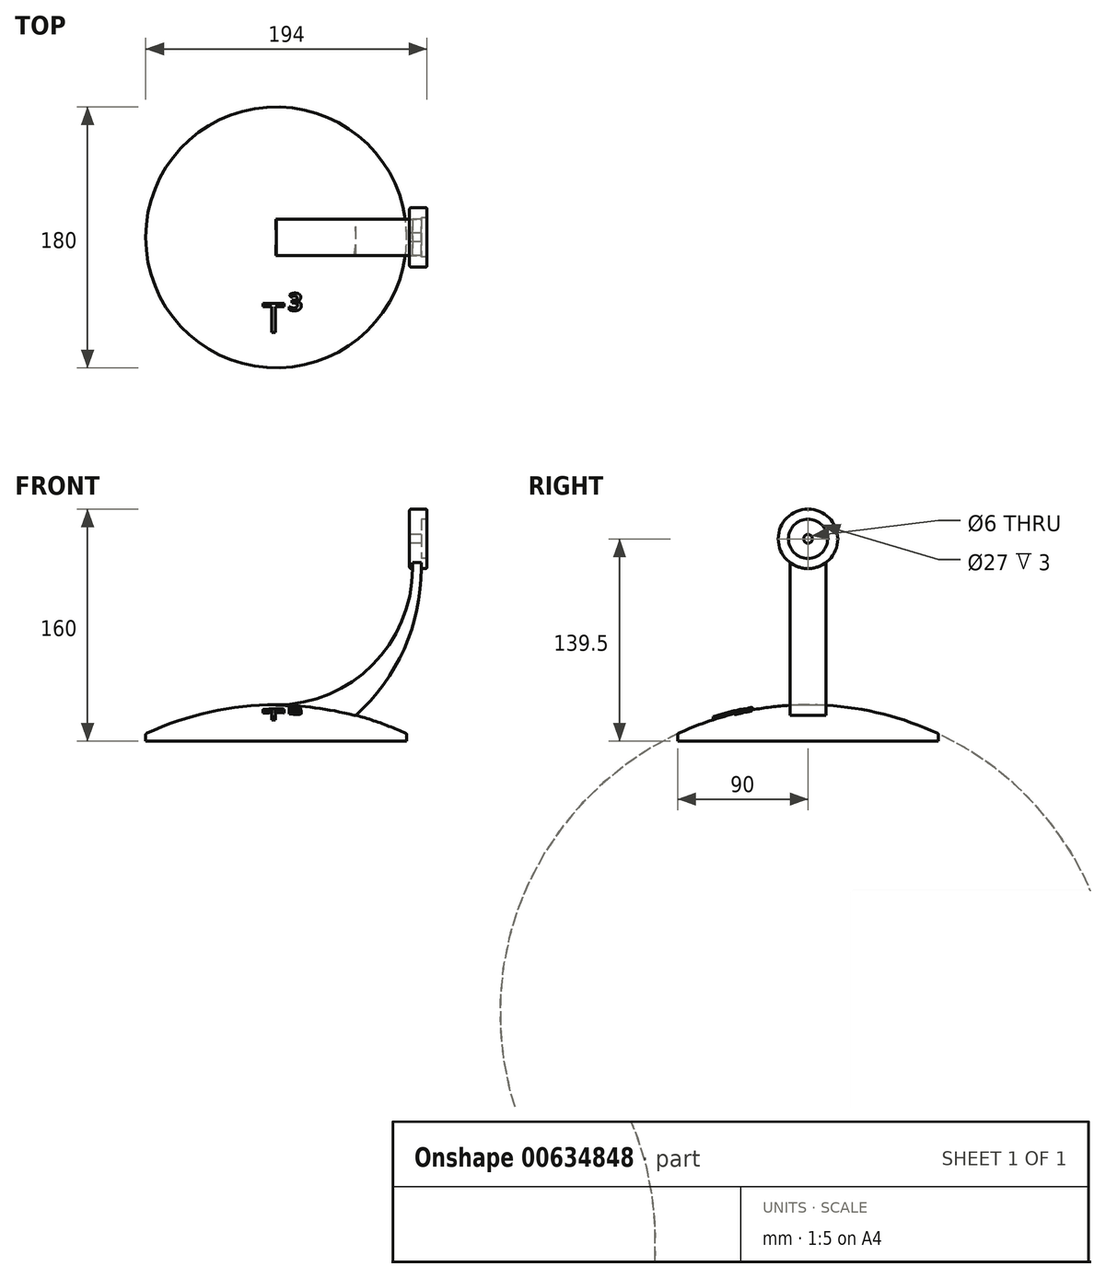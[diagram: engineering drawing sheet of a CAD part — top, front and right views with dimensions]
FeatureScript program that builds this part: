
annotation { "Feature Type Name" : "Feature", "Feature Type Description" : "" }
export const myFeature = defineFeature(function(context is Context, id is Id, definition is map)
    precondition{}
    {
        {
            var Q0;
            Q0=qCreatedBy(makeId("Front.planeOp"),FACE);
            var sketch = newSketch(context, id + "F0", { "sketchPlane" : qUnion([Q0])});
            skLineSegment(sketch, "E0", {"start": v(0, 0) * mm, "end": v(0, 71.2) * mm});
            skLineSegment(sketch, "E1", {"start": v(0, 0) * mm, "end": v(90, 0) * mm});
            skLineSegment(sketch, "E2", {"start": v(90, 0) * mm, "end": v(90, 5) * mm});
            skArc(sketch, "E3", {"start": v(90, 5) * mm, "mid": v(46.1, 19.94) * mm, "end": v(0, 25) * mm});
            skLineSegment(sketch, "E4", {"start": v(0, 25) * mm, "end": v(90, 25) * mm, "construction": true});
            skCircle(sketch, "E5", {"center": v(0, 139.5) * mm, "radius": 80 * mm, "construction": true});
            skCircle(sketch, "E6", {"center": v(0, 139.5) * mm, "radius": 114.5 * mm, "construction": true});
            skLineSegment(sketch, "E7", {"start": v(0, 139.5) * mm, "end": v(114.5, 139.5) * mm, "construction": true});
            skLineSegment(sketch, "E8.bottom", {"start": v(111.96, 139.5) * mm, "end": v(127.54, 139.5) * mm});
            skLineSegment(sketch, "E8.top", {"start": v(111.96, 137) * mm, "end": v(127.54, 137) * mm});
            skLineSegment(sketch, "E8.left", {"start": v(111.96, 139.5) * mm, "end": v(111.96, 137) * mm});
            skLineSegment(sketch, "E8.right", {"start": v(127.54, 139.5) * mm, "end": v(127.54, 137) * mm});
            skLineSegment(sketch, "E9", {"start": v(92, 137) * mm, "end": v(92, 119) * mm});
            skLineSegment(sketch, "E10", {"start": v(92, 119) * mm, "end": v(104, 119) * mm});
            skLineSegment(sketch, "E11", {"start": v(104, 119) * mm, "end": v(104, 126) * mm});
            skLineSegment(sketch, "E12", {"start": v(104, 126) * mm, "end": v(100, 126) * mm});
            skLineSegment(sketch, "E13", {"start": v(100, 126) * mm, "end": v(100, 137) * mm});
            skLineSegment(sketch, "E14", {"start": v(92, 136.5) * mm, "end": v(100, 136.5) * mm});
            skArc(sketch, "E15", {"start": v(0, 25) * mm, "mid": v(66.47, 52.53) * mm, "end": v(94, 119) * mm});
            skLineSegment(sketch, "E16", {"start": v(94, 119) * mm, "end": v(94, 136.5) * mm});
            skArc(sketch, "E17", {"start": v(55, 17.76) * mm, "mid": v(88.24, 63.6) * mm, "end": v(100, 119) * mm});
            skLineSegment(sketch, "E18", {"start": v(100, 126) * mm, "end": v(100, 119) * mm});
            skLineSegment(sketch, "E19", {"start": v(0, 25) * mm, "end": v(-9.19, 16.03) * mm});
            skLineSegment(sketch, "E20", {"start": v(-9.19, 16.03) * mm, "end": v(55, 17.76) * mm});
            skSolve(sketch);
        }
        {
            var Q0;
            {var subQ1=sQuery(id+"F0.wireOp",EDGE,"E10");Q0=makeQuery(id+"F0.imprint","IMPRINT",FACE,{"disambiguationData":[TD([[makeQuery(id+"F0.imprint","IMPRINT",EDGE,{"derivedFrom":subQ1}),1.0]])]});}
            var Q1;
            {var subQ3=sQuery(id+"F0.wireOp",EDGE,"E16");Q1=makeQuery(id+"F0.imprint","IMPRINT",FACE,{"disambiguationData":[TD([[makeQuery(id+"F0.imprint","IMPRINT",EDGE,{"derivedFrom":subQ3}),-1.0]])]});}
            var Q2;
            Q2=sQuery(id+"F0.wireOp",EDGE,"E7");
            revolve(context, id + "F1", {"entities" : qUnion([Q0, Q1]), "axis" : qUnion([Q2]), "revolveType" : RevolveType.FULL});
        }
        {
            var Q0;
            {var subQ0=sQuery(id+"F0.wireOp",EDGE,"E15");Q0=makeQuery(id+"F0.imprint","IMPRINT",FACE,{"disambiguationData":[TD([[makeQuery(id+"F0.imprint","IMPRINT",EDGE,{"derivedFrom":subQ0}),-1.0]])]});}
            var Q1;
            {var subQ3=sQuery(id+"F0.wireOp",EDGE,"E16");Q1=makeQuery(id+"F0.imprint","IMPRINT",FACE,{"disambiguationData":[TD([[makeQuery(id+"F0.imprint","IMPRINT",EDGE,{"derivedFrom":subQ3}),-1.0]])]});}
            var Q2;
            {var subQ0=sQuery(id+"F0.wireOp",EDGE,"iQjgoOAM-QroD-K7Jf-sKHi-gTNPPTzurfvL");Q2=makeQuery(id+"F0.imprint","IMPRINT",FACE,{"disambiguationData":[TD([[makeQuery(id+"F0.imprint","IMPRINT",EDGE,{"derivedFrom":subQ0}),1.0]])]});}
            var Q3;
            {var subQ0=sQuery(id+"F0.wireOp",EDGE,"E19");Q3=makeQuery(id+"F0.imprint","IMPRINT",FACE,{"disambiguationData":[TD([[makeQuery(id+"F0.imprint","IMPRINT",EDGE,{"derivedFrom":subQ0}),1.0]])]});}
            var Q4;
            {var subQ1=sQuery(id+"F0.wireOp",EDGE,"E0");var subQ3=sQuery(id+"F0.wireOp",EDGE,"E20");var subQ4=makeQuery(id+"F0.imprint","INTERSECT",VERTEX,{"derivedFrom":[subQ1,subQ3]});Q4=makeQuery(id+"F0.imprint","IMPRINT",FACE,{"disambiguationData":[TD([[makeQuery(id+"F0.imprint","IMPRINT",EDGE,{"disambiguationData":[TD([[subQ4,-1.0]])],"derivedFrom":subQ3}),1.0]])]});}
            extrude(context, id + "F2", {"entities" : qUnion([Q0, Q1, Q2, Q3, Q4]), "operationType" : NewBodyOperationType.ADD, "endBound" : BoundingType.SYMMETRIC, "depth" : 25 * mm, "offsetDistance" : 25 * mm});
        }
        {
            var Q0;
            {var subQ6=sQuery(id+"F0.wireOp",EDGE,"E1");Q0=makeQuery(id+"F0.imprint","IMPRINT",FACE,{"disambiguationData":[TD([[makeQuery(id+"F0.imprint","IMPRINT",EDGE,{"derivedFrom":subQ6}),1.0]])]});}
            var Q1;
            {var subQ1=sQuery(id+"F0.wireOp",EDGE,"E0");var subQ3=sQuery(id+"F0.wireOp",EDGE,"E20");var subQ4=makeQuery(id+"F0.imprint","INTERSECT",VERTEX,{"derivedFrom":[subQ1,subQ3]});Q1=makeQuery(id+"F0.imprint","IMPRINT",FACE,{"disambiguationData":[TD([[makeQuery(id+"F0.imprint","IMPRINT",EDGE,{"disambiguationData":[TD([[subQ4,-1.0]])],"derivedFrom":subQ3}),1.0]])]});}
            var Q2;
            Q2=sQuery(id+"F0.wireOp",EDGE,"E0");
            revolve(context, id + "F3", {"operationType" : NewBodyOperationType.ADD, "entities" : qUnion([Q0, Q1]), "axis" : qUnion([Q2]), "revolveType" : RevolveType.FULL});
        }
        {
            var Q0;
            Q0=qCreatedBy(makeId("Right.planeOp"),FACE);
            var sketch = newSketch(context, id + "F4", { "sketchPlane" : qUnion([Q0])});
            skArc(sketch, "E21", {"start": v(-12.5, 24.63) * mm, "mid": v(0, -400) * mm, "end": v(12.5, 24.63) * mm, "construction": true});
            skCircle(sketch, "E22", {"center": v(0, -187.5) * mm, "radius": 214.5 * mm});
            skLineSegment(sketch, "E23", {"start": v(-12.5, 24.63) * mm, "end": v(12.5, 24.63) * mm});
            skLineSegment(sketch, "E24", {"start": v(-19.73, 24.08) * mm, "end": v(-19.73, 26.1) * mm});
            skLineSegment(sketch, "E25", {"start": v(-85.59, 7) * mm, "end": v(-86.7, 8.7) * mm});
            skLineSegment(sketch, "E26", {"start": v(88.58, 5.66) * mm, "end": v(89.58, 7.4) * mm});
            skLineSegment(sketch, "E27", {"start": v(24.67, 23.56) * mm, "end": v(25.62, 25.46) * mm});
            skCircle(sketch, "E28", {"center": v(0, -187.5) * mm, "radius": 281.34 * mm});
            skLineSegment(sketch, "E29", {"start": v(-19.73, 26.1) * mm, "end": v(-28.75, 92.36) * mm});
            skLineSegment(sketch, "E30", {"start": v(-86.7, 8.7) * mm, "end": v(-111.68, 70.72) * mm});
            skLineSegment(sketch, "E31", {"start": v(25.62, 25.46) * mm, "end": v(39.33, 91.07) * mm});
            skLineSegment(sketch, "E32", {"start": v(39.33, 91.07) * mm, "end": v(120.16, 66.88) * mm});
            skLineSegment(sketch, "E33", {"start": v(120.16, 66.88) * mm, "end": v(89.58, 7.4) * mm});
            skSolve(sketch);
        }
        {
            var Q0;
            Q0=qCreatedBy(makeId("Top.planeOp"),FACE);
            var sketch = newSketch(context, id + "F5", { "sketchPlane" : qUnion([Q0])});
            skText(sketch, "E34", { "text": "T", "fontName": "NotoSans-Regular.ttf"});
            skText(sketch, "E35", { "text": "3", "fontName": "OpenSans-Bold.ttf"});
            const initialGuessF5  = {"E34": [-0.00951, -0.0655, 1, 0, 0.02], "E35": [0.00843, -0.0505, 1, 0, 0.012]};
            skSetInitialGuess(sketch, initialGuessF5);
            skSolve(sketch);
        }
        {
            var Q0;
            Q0 = qSketchRegion(id + "F5", true);
            extrude(context, id + "F6", {"entities" : qUnion([Q0]), "operationType" : NewBodyOperationType.ADD, "depth" : 25 * mm, "offsetDistance" : 25 * mm});
        }
        {
            var Q0;
            {var subQ0=sQuery(id+"F4.wireOp",EDGE,"E29");Q0=makeQuery(id+"F4.imprint","IMPRINT",FACE,{"disambiguationData":[TD([[makeQuery(id+"F4.imprint","IMPRINT",EDGE,{"derivedFrom":subQ0}),1.0]])]});}
            var Q1;
            {var subQ2=sQuery(id+"F4.wireOp",EDGE,"E31");Q1=makeQuery(id+"F4.imprint","IMPRINT",FACE,{"disambiguationData":[TD([[makeQuery(id+"F4.imprint","IMPRINT",EDGE,{"derivedFrom":subQ2}),-1.0]])]});}
            var Q2;
            Q2=sQuery(id+"F0.wireOp",EDGE,"E0");
            revolve(context, id + "F7", {"operationType" : NewBodyOperationType.REMOVE, "entities" : qUnion([Q0, Q1]), "axis" : qUnion([Q2]), "revolveType" : RevolveType.SYMMETRIC, "oppositeDirection" : true, "angle" : 70 * degree});
        }
        {
            var Q0;
            Q0=makeQuery(id+"F1.opRevolve","SWEPT_EDGE",EDGE,{"disambiguationData":[OSD([sQuery(id+"F0.wireOp",EDGE,"E10"),sQuery(id+"F0.wireOp",EDGE,"E11")])]});
            var Q1;
            Q1=makeQuery(id+"F1.opRevolve","SWEPT_EDGE",EDGE,{"disambiguationData":[OSD([sQuery(id+"F0.wireOp",EDGE,"E11"),sQuery(id+"F0.wireOp",EDGE,"E12")])]});
            var Q2;
            Q2=makeQuery(id+"FUaVH2AzZwELlac_1.1.F1.opRevolve","SWEPT_EDGE",EDGE,{"disambiguationData":[OSD([sQuery(id+"F0.wireOp",EDGE,"E10"),sQuery(id+"F0.wireOp",EDGE,"E11")])]});
            var Q3;
            Q3=makeQuery(id+"FUaVH2AzZwELlac_1.1.F1.opRevolve","SWEPT_EDGE",EDGE,{"disambiguationData":[OSD([sQuery(id+"F0.wireOp",EDGE,"E9"),sQuery(id+"F0.wireOp",EDGE,"E10")])]});
            var Q4;
            Q4=makeQuery(id+"F1.opRevolve","SWEPT_EDGE",EDGE,{"disambiguationData":[OSD([sQuery(id+"F0.wireOp",EDGE,"E9"),sQuery(id+"F0.wireOp",EDGE,"E10")])]});
            var Q5;
            Q5=makeQuery(id+"F3.opRevolve","SWEPT_EDGE",EDGE,{"disambiguationData":[OSD([sQuery(id+"F0.wireOp",EDGE,"E2"),sQuery(id+"F0.wireOp",EDGE,"E3")])]});
            var Q6;
            Q6=makeQuery(id+"FUaVH2AzZwELlac_1.1.F1.opRevolve","SWEPT_EDGE",EDGE,{"disambiguationData":[OSD([sQuery(id+"F0.wireOp",EDGE,"E11"),sQuery(id+"F0.wireOp",EDGE,"E12")])]});
            fillet(context, id + "F8", {"entities" : qUnion([Q0, Q1, Q2, Q3, Q4, Q5, Q6]), "radius" : 1 * mm, "tangentPropagation" : true, "allowEdgeOverflow" : false});
        }
    });
